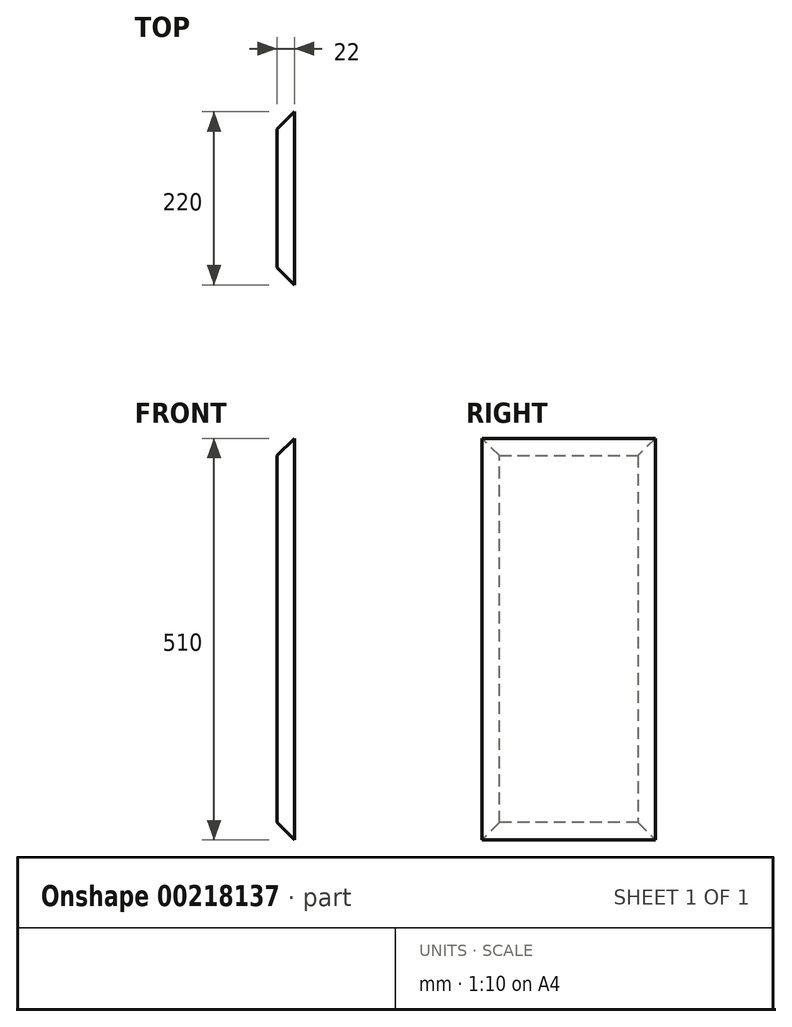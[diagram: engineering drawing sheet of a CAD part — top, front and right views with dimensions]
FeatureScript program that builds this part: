
annotation { "Feature Type Name" : "Feature", "Feature Type Description" : "" }
export const myFeature = defineFeature(function(context is Context, id is Id, definition is map)
    precondition{}
    {
        {
            var Q0;
            Q0=qCreatedBy(makeId("Right.planeOp"),FACE);
            var sketch = newSketch(context, id + "F0", { "sketchPlane" : qUnion([Q0])});
            skLineSegment(sketch, "E0.bottom", {"start": v(110, 255) * mm, "end": v(-110, 255) * mm});
            skLineSegment(sketch, "E0.top", {"start": v(110, -255) * mm, "end": v(-110, -255) * mm});
            skLineSegment(sketch, "E0.left", {"start": v(110, 255) * mm, "end": v(110, -255) * mm});
            skLineSegment(sketch, "E0.right", {"start": v(-110, 255) * mm, "end": v(-110, -255) * mm});
            skPoint(sketch, "E0.middle", {"position": v(0, 0) * mm});
            skSolve(sketch);
        }
        {
            var Q0;
            Q0 = qSketchRegion(id + "F0", true);
            var Q1;
            Q1=makeQuery(id+"F0.imprint","IMPRINT",FACE,{"disambiguationData":[TD([[makeQuery(id+"F0.imprint","IMPRINT",EDGE,{"derivedFrom":sQuery(id+"F0.wireOp",EDGE,"E0.bottom")}),1.0]])]});
            extrude(context, id + "F1", {"entities" : qUnion([Q0, Q1]), "depth" : 22 * mm});
        }
        {
            var Q0;
            Q0=makeQuery(id+"F1.opExtrude","CAP_EDGE",EDGE,{"disambiguationData":[OSD([sQuery(id+"F0.wireOp",EDGE,"E0.bottom")])],"isStart":true});
            var Q1;
            Q1=makeQuery(id+"F1.opExtrude","CAP_EDGE",EDGE,{"disambiguationData":[OSD([sQuery(id+"F0.wireOp",EDGE,"E0.left")])],"isStart":true});
            var Q2;
            Q2=makeQuery(id+"F1.opExtrude","CAP_EDGE",EDGE,{"disambiguationData":[OSD([sQuery(id+"F0.wireOp",EDGE,"E0.top")])],"isStart":true});
            var Q3;
            Q3=makeQuery(id+"F1.opExtrude","CAP_EDGE",EDGE,{"disambiguationData":[OSD([sQuery(id+"F0.wireOp",EDGE,"E0.right")])],"isStart":true});
            chamfer(context, id + "F2", {"entities" : qUnion([Q0, Q1, Q2, Q3]), "width" : 22 * mm, "tangentPropagation" : true});
        }
    });
